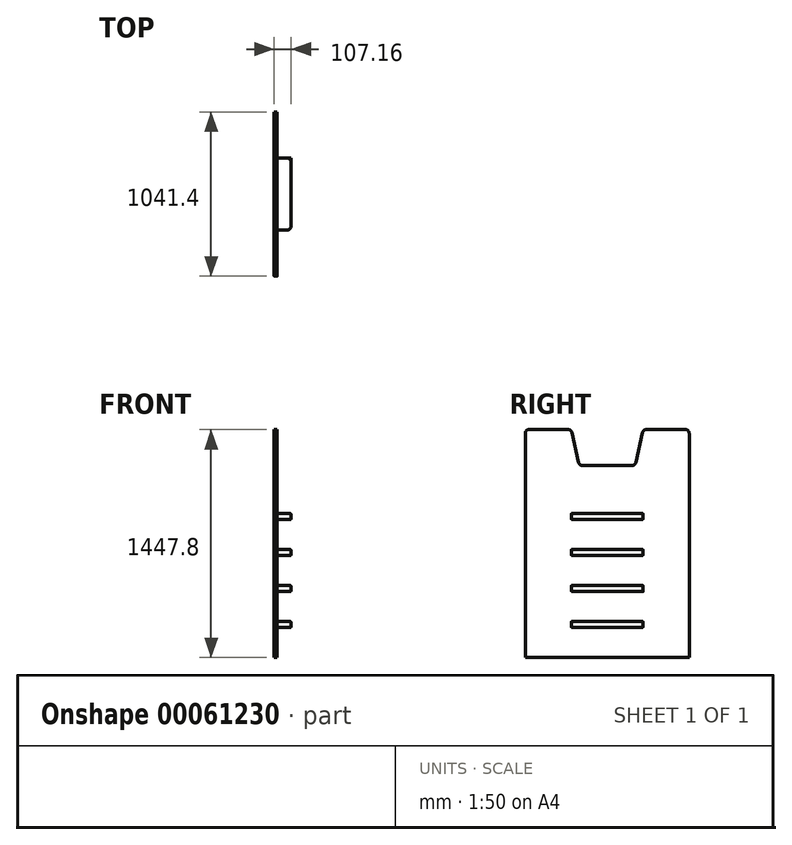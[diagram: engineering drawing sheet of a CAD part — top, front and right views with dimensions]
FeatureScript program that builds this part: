
annotation { "Feature Type Name" : "Feature", "Feature Type Description" : "" }
export const myFeature = defineFeature(function(context is Context, id is Id, definition is map)
    precondition{}
    {
        {
            var Q0;
            Q0=qCreatedBy(makeId("Right.planeOp"),FACE);
            var sketch = newSketch(context, id + "F0", { "sketchPlane" : qUnion([Q0])});
            skLineSegment(sketch, "E0.bottom", {"start": v(0, 0) * mm, "end": v(1041.4, 0) * mm});
            skLineSegment(sketch, "E0.top", {"start": v(25.4, 1447.8) * mm, "end": v(271.72, 1447.8) * mm});
            skLineSegment(sketch, "E0.left", {"start": v(0, 0) * mm, "end": v(0, 1422.4) * mm});
            skLineSegment(sketch, "E0.right", {"start": v(1041.4, 0) * mm, "end": v(1041.4, 1422.4) * mm});
            skLineSegment(sketch, "E1", {"start": v(0, 914.4) * mm, "end": v(1041.4, 914.4) * mm, "construction": true});
            skLineSegment(sketch, "E2", {"start": v(520.7, 1447.8) * mm, "end": v(520.7, 0) * mm, "construction": true});
            skPoint(sketch, "E3.visualSharp", {"position": v(0, 1447.8) * mm});
            skArc(sketch, "E3.filletArc", {"start": v(25.4, 1447.8) * mm, "mid": v(7.44, 1440.36) * mm, "end": v(0, 1422.4) * mm});
            skPoint(sketch, "E4.visualSharp", {"position": v(1041.4, 1447.8) * mm});
            skArc(sketch, "E4.filletArc", {"start": v(1041.4, 1422.4) * mm, "mid": v(1033.96, 1440.36) * mm, "end": v(1016, 1447.8) * mm});
            skLineSegment(sketch, "E5.0", {"start": v(292.1, 1447.8) * mm, "end": v(292.1, 0) * mm, "construction": true});
            skLineSegment(sketch, "E6.0", {"start": v(749.3, 1447.8) * mm, "end": v(749.3, 0) * mm, "construction": true});
            skLineSegment(sketch, "E7.0", {"start": v(0, 1219.2) * mm, "end": v(1041.4, 1219.2) * mm, "construction": true});
            skLineSegment(sketch, "E8.0", {"start": v(342.9, 1447.8) * mm, "end": v(342.9, 0) * mm, "construction": true});
            skLineSegment(sketch, "E9.0", {"start": v(698.5, 1447.8) * mm, "end": v(698.5, 0) * mm, "construction": true});
            skLineSegment(sketch, "E10", {"start": v(296.52, 1427.91) * mm, "end": v(338.48, 1239.09) * mm});
            skLineSegment(sketch, "E11", {"start": v(363.28, 1219.2) * mm, "end": v(678.12, 1219.2) * mm});
            skLineSegment(sketch, "E12", {"start": v(702.92, 1239.09) * mm, "end": v(744.88, 1427.91) * mm});
            skLineSegment(sketch, "E13.trimOffspring", {"start": v(769.68, 1447.8) * mm, "end": v(1016, 1447.8) * mm});
            skPoint(sketch, "E14.visualSharp", {"position": v(292.1, 1447.8) * mm});
            skArc(sketch, "E14.filletArc", {"start": v(296.52, 1427.91) * mm, "mid": v(287.62, 1442.21) * mm, "end": v(271.72, 1447.8) * mm});
            skPoint(sketch, "E15.visualSharp", {"position": v(342.9, 1219.2) * mm});
            skArc(sketch, "E15.filletArc", {"start": v(338.48, 1239.09) * mm, "mid": v(347.38, 1224.79) * mm, "end": v(363.28, 1219.2) * mm});
            skPoint(sketch, "E16.visualSharp", {"position": v(698.5, 1219.2) * mm});
            skArc(sketch, "E16.filletArc", {"start": v(678.12, 1219.2) * mm, "mid": v(694.02, 1224.79) * mm, "end": v(702.92, 1239.09) * mm});
            skPoint(sketch, "E17.visualSharp", {"position": v(749.3, 1447.8) * mm});
            skArc(sketch, "E17.filletArc", {"start": v(769.68, 1447.8) * mm, "mid": v(753.78, 1442.21) * mm, "end": v(744.88, 1427.91) * mm});
            skSolve(sketch);
        }
        {
            var Q0;
            Q0 = qSketchRegion(id + "F0", true);
            extrude(context, id + "F1", {"entities" : qUnion([Q0]), "depth" : 18.26 * mm});
        }
        {
            var Q0;
            Q0=makeQuery(id+"F1.opExtrude","CAP_FACE",FACE,{"disambiguationData":[OSD([sQuery(id+"F0.wireOp",EDGE,"E0.bottom"),sQuery(id+"F0.wireOp",EDGE,"E0.top"),sQuery(id+"F0.wireOp",EDGE,"E0.left"),sQuery(id+"F0.wireOp",EDGE,"E0.right"),sQuery(id+"F0.wireOp",EDGE,"E3.filletArc"),sQuery(id+"F0.wireOp",EDGE,"E4.filletArc"),sQuery(id+"F0.wireOp",EDGE,"E10"),sQuery(id+"F0.wireOp",EDGE,"E11"),sQuery(id+"F0.wireOp",EDGE,"E12"),sQuery(id+"F0.wireOp",EDGE,"E13.trimOffspring"),sQuery(id+"F0.wireOp",EDGE,"E14.filletArc"),sQuery(id+"F0.wireOp",EDGE,"E15.filletArc"),sQuery(id+"F0.wireOp",EDGE,"E16.filletArc"),sQuery(id+"F0.wireOp",EDGE,"E17.filletArc")])],"isStart":false});
            var sketch = newSketch(context, id + "F2", { "sketchPlane" : qUnion([Q0])});
            skLineSegment(sketch, "E18.bottom", {"start": v(292.1, 228.6) * mm, "end": v(749.3, 228.6) * mm});
            skLineSegment(sketch, "E18.top", {"start": v(292.1, 190.5) * mm, "end": v(749.3, 190.5) * mm});
            skLineSegment(sketch, "E18.left", {"start": v(292.1, 228.6) * mm, "end": v(292.1, 190.5) * mm});
            skLineSegment(sketch, "E18.right", {"start": v(749.3, 228.6) * mm, "end": v(749.3, 190.5) * mm});
            skLineSegment(sketch, "E19.bottom", {"start": v(292.1, 457.2) * mm, "end": v(749.3, 457.2) * mm});
            skLineSegment(sketch, "E19.top", {"start": v(292.1, 419.1) * mm, "end": v(749.3, 419.1) * mm});
            skLineSegment(sketch, "E19.left", {"start": v(292.1, 457.2) * mm, "end": v(292.1, 419.1) * mm});
            skLineSegment(sketch, "E19.right", {"start": v(749.3, 457.2) * mm, "end": v(749.3, 419.1) * mm});
            skLineSegment(sketch, "E20.bottom", {"start": v(292.1, 685.8) * mm, "end": v(749.3, 685.8) * mm});
            skLineSegment(sketch, "E20.top", {"start": v(292.1, 647.7) * mm, "end": v(749.3, 647.7) * mm});
            skLineSegment(sketch, "E20.left", {"start": v(292.1, 685.8) * mm, "end": v(292.1, 647.7) * mm});
            skLineSegment(sketch, "E20.right", {"start": v(749.3, 685.8) * mm, "end": v(749.3, 647.7) * mm});
            skLineSegment(sketch, "E21.bottom", {"start": v(292.1, 914.4) * mm, "end": v(749.3, 914.4) * mm});
            skLineSegment(sketch, "E21.top", {"start": v(292.1, 876.3) * mm, "end": v(749.3, 876.3) * mm});
            skLineSegment(sketch, "E21.left", {"start": v(292.1, 914.4) * mm, "end": v(292.1, 876.3) * mm});
            skLineSegment(sketch, "E21.right", {"start": v(749.3, 914.4) * mm, "end": v(749.3, 876.3) * mm});
            skLineSegment(sketch, "E22", {"start": v(520.7, 1219.2) * mm, "end": v(520.7, 0) * mm, "construction": true});
            skLineSegment(sketch, "E23", {"start": v(0, 914.4) * mm, "end": v(1041.4, 914.4) * mm, "construction": true});
            skSolve(sketch);
        }
        {
            var Q0;
            Q0 = qSketchRegion(id + "F2", true);
            extrude(context, id + "F3", {"entities" : qUnion([Q0]), "operationType" : NewBodyOperationType.ADD, "depth" : 88.9 * mm});
        }
        {
            var Q0;
            Q0=makeQuery(id+"F3.opExtrude","CAP_EDGE",EDGE,{"disambiguationData":[OSD([sQuery(id+"F2.wireOp",EDGE,"E21.left")])],"isStart":false});
            var Q1;
            Q1=makeQuery(id+"F3.opExtrude","CAP_EDGE",EDGE,{"disambiguationData":[OSD([sQuery(id+"F2.wireOp",EDGE,"E21.right")])],"isStart":false});
            var Q2;
            Q2=makeQuery(id+"F3.opExtrude","CAP_EDGE",EDGE,{"disambiguationData":[OSD([sQuery(id+"F2.wireOp",EDGE,"E20.left")])],"isStart":false});
            var Q3;
            Q3=makeQuery(id+"F3.opExtrude","CAP_EDGE",EDGE,{"disambiguationData":[OSD([sQuery(id+"F2.wireOp",EDGE,"E20.right")])],"isStart":false});
            var Q4;
            Q4=makeQuery(id+"F3.opExtrude","CAP_EDGE",EDGE,{"disambiguationData":[OSD([sQuery(id+"F2.wireOp",EDGE,"E19.left")])],"isStart":false});
            var Q5;
            Q5=makeQuery(id+"F3.opExtrude","CAP_EDGE",EDGE,{"disambiguationData":[OSD([sQuery(id+"F2.wireOp",EDGE,"E18.left")])],"isStart":false});
            var Q6;
            Q6=makeQuery(id+"F3.opExtrude","CAP_EDGE",EDGE,{"disambiguationData":[OSD([sQuery(id+"F2.wireOp",EDGE,"E18.right")])],"isStart":false});
            fillet(context, id + "F4", {"entities" : qUnion([Q0, Q1, Q2, Q3, Q4, Q5, Q6]), "radius" : 25.4 * mm, "tangentPropagation" : true, "allowEdgeOverflow" : false});
        }
        {
            var Q0;
            Q0=makeQuery(id+"F3.opExtrude","SWEPT_EDGE",EDGE,{"disambiguationData":[OSD([sQuery(id+"F2.wireOp",EDGE,"E21.bottom"),sQuery(id+"F2.wireOp",EDGE,"E21.left")])]});
            var Q1;
            Q1=makeQuery(id+"F3.opExtrude","SWEPT_EDGE",EDGE,{"disambiguationData":[OSD([sQuery(id+"F2.wireOp",EDGE,"E21.top"),sQuery(id+"F2.wireOp",EDGE,"E21.left")])]});
            var Q2;
            Q2=makeQuery(id+"F3.opExtrude","SWEPT_EDGE",EDGE,{"disambiguationData":[OSD([sQuery(id+"F2.wireOp",EDGE,"E20.bottom"),sQuery(id+"F2.wireOp",EDGE,"E20.left")])]});
            var Q3;
            Q3=makeQuery(id+"F3.opExtrude","SWEPT_EDGE",EDGE,{"disambiguationData":[OSD([sQuery(id+"F2.wireOp",EDGE,"E20.top"),sQuery(id+"F2.wireOp",EDGE,"E20.left")])]});
            var Q4;
            Q4=makeQuery(id+"F3.opExtrude","SWEPT_EDGE",EDGE,{"disambiguationData":[OSD([sQuery(id+"F2.wireOp",EDGE,"E19.bottom"),sQuery(id+"F2.wireOp",EDGE,"E19.left")])]});
            var Q5;
            Q5=makeQuery(id+"F3.opExtrude","SWEPT_EDGE",EDGE,{"disambiguationData":[OSD([sQuery(id+"F2.wireOp",EDGE,"E19.top"),sQuery(id+"F2.wireOp",EDGE,"E19.left")])]});
            var Q6;
            Q6=makeQuery(id+"F3.opExtrude","SWEPT_EDGE",EDGE,{"disambiguationData":[OSD([sQuery(id+"F2.wireOp",EDGE,"E18.bottom"),sQuery(id+"F2.wireOp",EDGE,"E18.left")])]});
            var Q7;
            Q7=makeQuery(id+"F3.opExtrude","SWEPT_EDGE",EDGE,{"disambiguationData":[OSD([sQuery(id+"F2.wireOp",EDGE,"E18.top"),sQuery(id+"F2.wireOp",EDGE,"E18.left")])]});
            fillet(context, id + "F5", {"entities" : qUnion([Q0, Q1, Q2, Q3, Q4, Q5, Q6, Q7]), "radius" : 6.35 * mm, "tangentPropagation" : true, "allowEdgeOverflow" : false});
        }
    });
